# Revit family: YVSE-650
name_source: partatom
category: 配管付属品
revit_build: Autodesk Revit 2018 (Build: 20170223_1515(x64)
units: mm (PartAtom-declared; Revit-internal decimal feet)

## family parameters
OmniClass タイトル = Mixing Valves for Liquid Services
OmniClass 番号 = 23.65.55.14.24
パーツ タイプ = 標準
ロード時にボイドで切り取り = いいえ
丸型コネクタ寸法 = 直径を使用
作業面ベース = いいえ
共有 = いいえ
常に垂直 = はい

## types (1)
- YVSE-650
    OmniClassCode = 23-65 55 14 24
    URL = https://www.yamatoprotec.co.jp
    Uniclass2015Code = Pr_70_55_33_30
    Uniclass2015Title = Foam sprinklers
    Uniclass2015Version = Systems v1.9
    アセンブリ コード = D4090200
    キーノート = 13910
    モデル = YVSE-650
    仕様書バージョン = Version1.0
    企業コード = 580077214
    使用圧力範囲 = 0.98 - 1.47Mpa
    分類コード = 50903001800000
    取付方向 = 横型用
    圧力損失等価管長 = 0  [stored 0 ft]
    最大流量(L/min) = 0
    積算_科目 = 9 消化設備
    製造元 = ヤマトプロテック株式会社
    説明 = YVSE-650

note: [stored X ft] marks values corroborated as IEEE doubles in the binary element streams (Revit-internal decimal feet)
